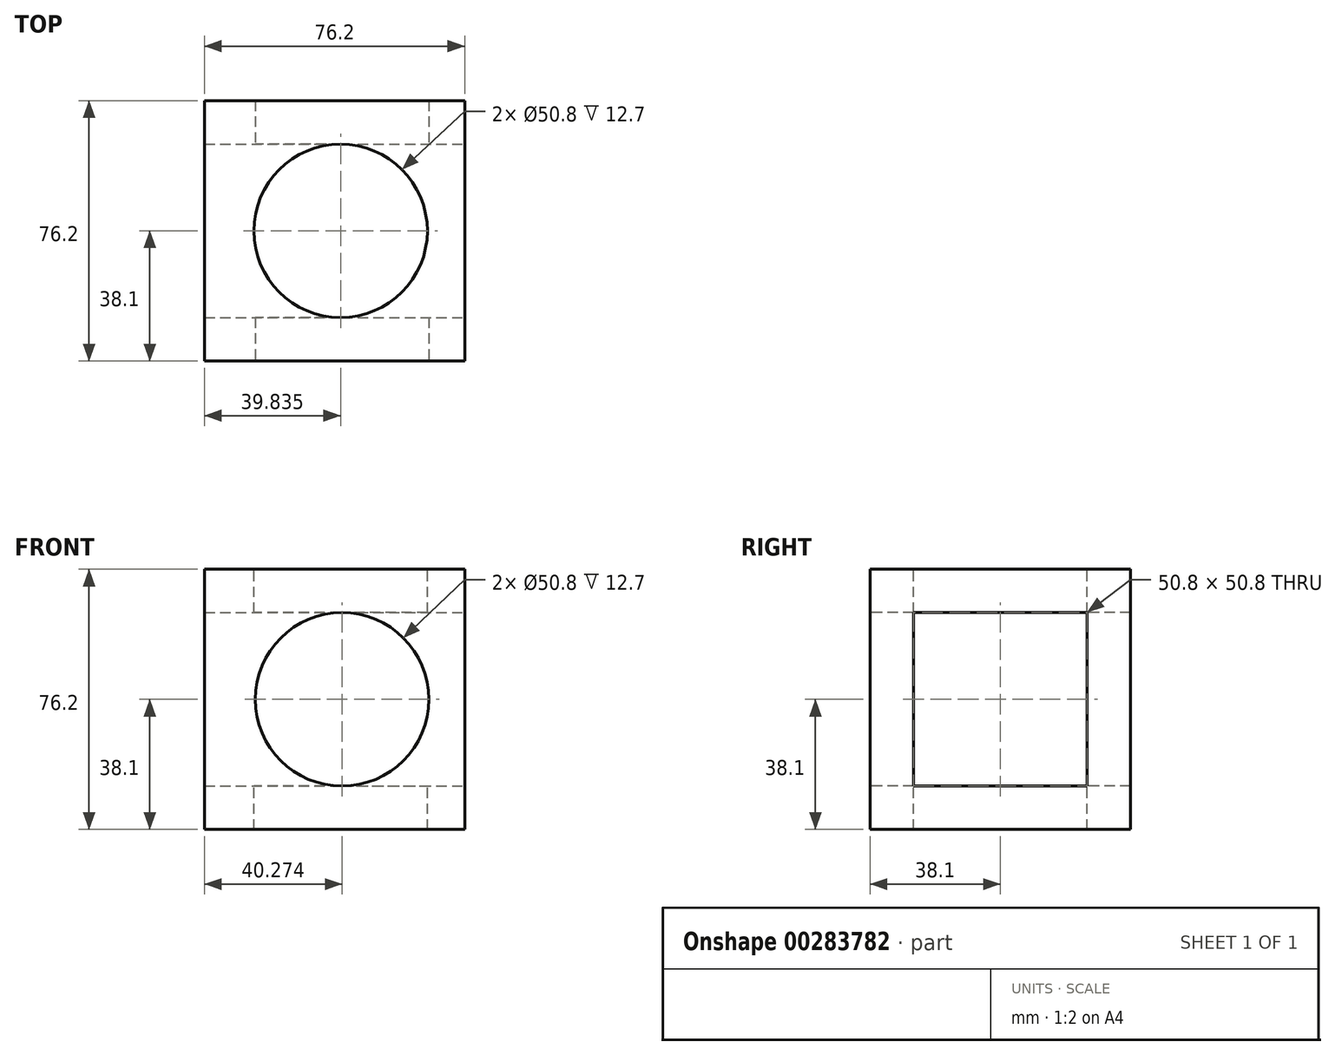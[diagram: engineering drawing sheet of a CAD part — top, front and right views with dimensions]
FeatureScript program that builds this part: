
annotation { "Feature Type Name" : "Feature", "Feature Type Description" : "" }
export const myFeature = defineFeature(function(context is Context, id is Id, definition is map)
    precondition{}
    {
        {
            var Q0;
            Q0=qCreatedBy(makeId("Front.planeOp"),FACE);
            var sketch = newSketch(context, id + "F0", { "sketchPlane" : qUnion([Q0])});
            skLineSegment(sketch, "E0.bottom", {"start": v(38.1, 38.1) * mm, "end": v(-38.1, 38.1) * mm});
            skLineSegment(sketch, "E0.top", {"start": v(38.1, -38.1) * mm, "end": v(-38.1, -38.1) * mm});
            skLineSegment(sketch, "E0.left", {"start": v(38.1, 38.1) * mm, "end": v(38.1, -38.1) * mm});
            skLineSegment(sketch, "E0.right", {"start": v(-38.1, 38.1) * mm, "end": v(-38.1, -38.1) * mm});
            skPoint(sketch, "E0.middle", {"position": v(0, 0) * mm});
            skSolve(sketch);
        }
        {
            var Q0;
            Q0=makeQuery(id+"F0.imprint","IMPRINT",FACE,{"disambiguationData":[TD([[makeQuery(id+"F0.imprint","IMPRINT",EDGE,{"derivedFrom":sQuery(id+"F0.wireOp",EDGE,"E0.bottom")}),1.0]])]});
            extrude(context, id + "F1", {"entities" : qUnion([Q0]), "endBound" : BoundingType.SYMMETRIC, "depth" : 76.2 * mm});
        }
        {
            var Q0;
            Q0=makeQuery(id+"F1.opExtrude","CAP_FACE",FACE,{"disambiguationData":[OSD([sQuery(id+"F0.wireOp",EDGE,"E0.bottom"),sQuery(id+"F0.wireOp",EDGE,"E0.top"),sQuery(id+"F0.wireOp",EDGE,"E0.left"),sQuery(id+"F0.wireOp",EDGE,"E0.right")])],"isStart":false});
            var sketch = newSketch(context, id + "F2", { "sketchPlane" : qUnion([Q0])});
            skCircle(sketch, "E1", {"center": v(2.17, 0) * mm, "radius": 25.4 * mm});
            skSolve(sketch);
        }
        {
            var Q0;
            Q0=makeQuery(id+"F2.imprint","IMPRINT",FACE,{"disambiguationData":[TD([[makeQuery(id+"F2.imprint","IMPRINT",EDGE,{"derivedFrom":sQuery(id+"F2.wireOp",EDGE,"E1")}),1.0]])]});
            extrude(context, id + "F3", {"entities" : qUnion([Q0]), "operationType" : NewBodyOperationType.REMOVE, "oppositeDirection" : true, "depth" : 101.6 * mm});
        }
        {
            var Q0;
            Q0=makeQuery(id+"F1.opExtrude","SWEPT_FACE",FACE,{"disambiguationData":[OSD([sQuery(id+"F0.wireOp",EDGE,"E0.bottom")])]});
            var sketch = newSketch(context, id + "F4", { "sketchPlane" : qUnion([Q0])});
            skCircle(sketch, "E2", {"center": v(1.74, 0) * mm, "radius": 25.4 * mm});
            skSolve(sketch);
        }
        {
            var Q0;
            Q0=makeQuery(id+"F4.imprint","IMPRINT",FACE,{"disambiguationData":[TD([[makeQuery(id+"F4.imprint","IMPRINT",EDGE,{"derivedFrom":sQuery(id+"F4.wireOp",EDGE,"E2")}),1.0]])]});
            extrude(context, id + "F5", {"entities" : qUnion([Q0]), "operationType" : NewBodyOperationType.REMOVE, "oppositeDirection" : true, "depth" : 101.6 * mm});
        }
        {
            var Q0;
            Q0=makeQuery(id+"F1.opExtrude","SWEPT_FACE",FACE,{"disambiguationData":[OSD([sQuery(id+"F0.wireOp",EDGE,"E0.left")])]});
            var sketch = newSketch(context, id + "F6", { "sketchPlane" : qUnion([Q0])});
            skLineSegment(sketch, "E3.bottom", {"start": v(25.4, -25.4) * mm, "end": v(-25.4, -25.4) * mm});
            skLineSegment(sketch, "E3.top", {"start": v(25.4, 25.4) * mm, "end": v(-25.4, 25.4) * mm});
            skLineSegment(sketch, "E3.left", {"start": v(25.4, -25.4) * mm, "end": v(25.4, 25.4) * mm});
            skLineSegment(sketch, "E3.right", {"start": v(-25.4, -25.4) * mm, "end": v(-25.4, 25.4) * mm});
            skPoint(sketch, "E3.middle", {"position": v(0, 0) * mm});
            skSolve(sketch);
        }
        {
            var Q0;
            Q0=makeQuery(id+"F6.imprint","IMPRINT",FACE,{"disambiguationData":[TD([[makeQuery(id+"F6.imprint","IMPRINT",EDGE,{"derivedFrom":sQuery(id+"F6.wireOp",EDGE,"E3.bottom")}),-1.0]])]});
            extrude(context, id + "F7", {"entities" : qUnion([Q0]), "operationType" : NewBodyOperationType.REMOVE, "oppositeDirection" : true, "depth" : 101.6 * mm});
        }
    });
